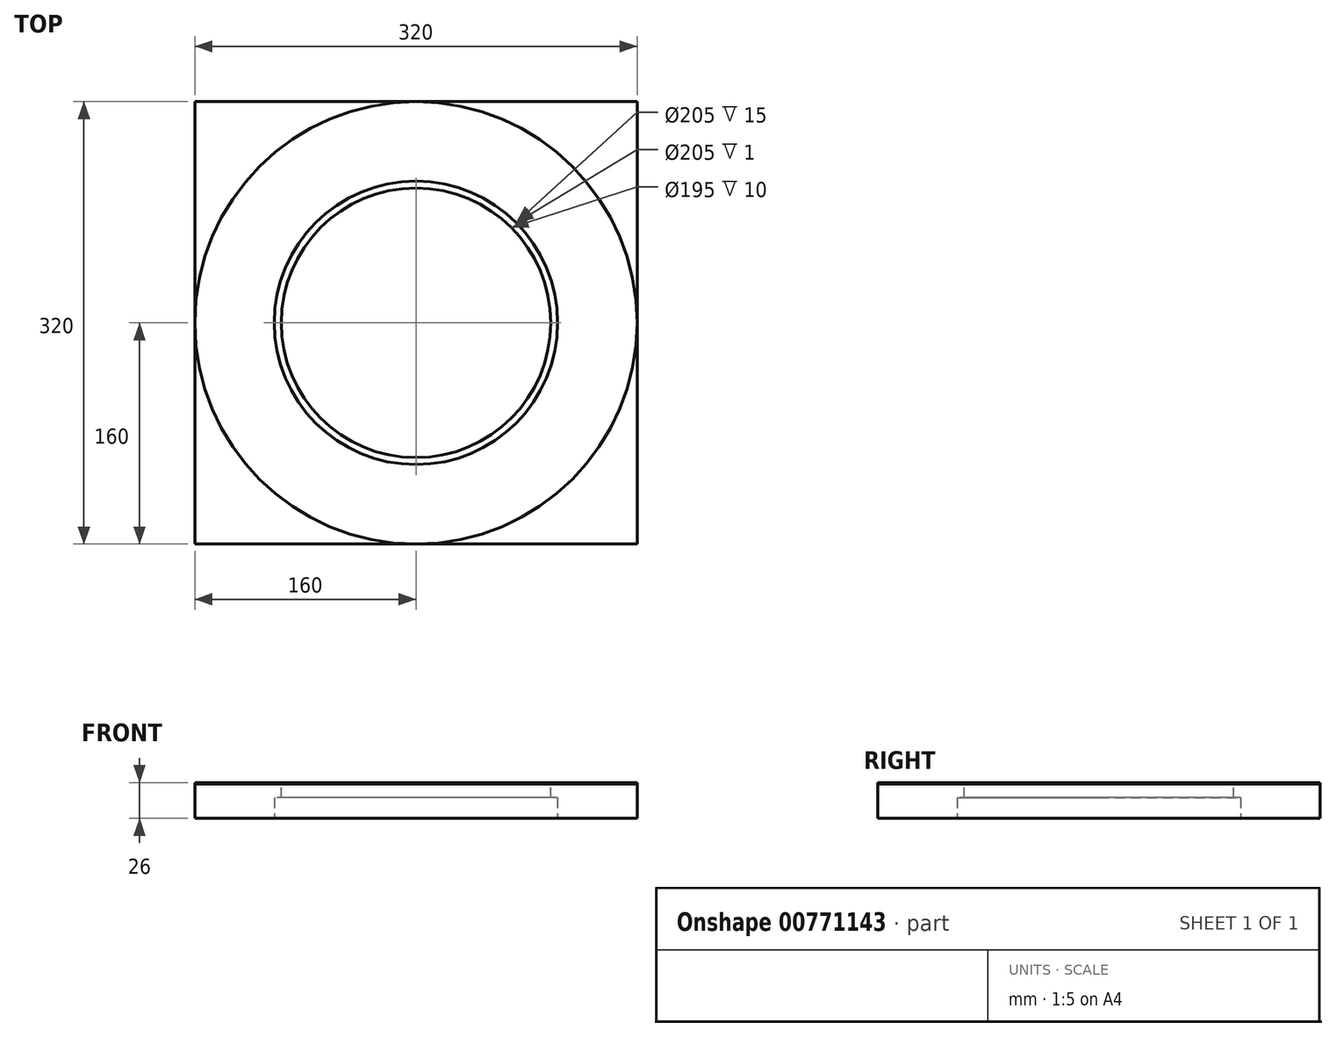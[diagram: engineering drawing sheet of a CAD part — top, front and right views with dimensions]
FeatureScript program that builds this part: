
annotation { "Feature Type Name" : "Feature", "Feature Type Description" : "" }
export const myFeature = defineFeature(function(context is Context, id is Id, definition is map)
    precondition{}
    {
        {
            var Q0;
            Q0=qCreatedBy(makeId("Top.planeOp"),FACE);
            var sketch = newSketch(context, id + "F0", { "sketchPlane" : qUnion([Q0])});
            skLineSegment(sketch, "E0.bottom", {"start": v(-160, 160) * mm, "end": v(160, 160) * mm});
            skLineSegment(sketch, "E0.top", {"start": v(-160, -160) * mm, "end": v(160, -160) * mm});
            skLineSegment(sketch, "E0.left", {"start": v(-160, 160) * mm, "end": v(-160, -160) * mm});
            skLineSegment(sketch, "E0.right", {"start": v(160, 160) * mm, "end": v(160, -160) * mm});
            skPoint(sketch, "E0.middle", {"position": v(0, 0) * mm});
            skCircle(sketch, "E1", {"center": v(0, 0) * mm, "radius": 102.5 * mm});
            skCircle(sketch, "E2", {"center": v(0, 0) * mm, "radius": 160 * mm});
            skSolve(sketch);
        }
        {
            var Q0;
            {var subQ0=sQuery(id+"F0.wireOp",EDGE,"E0.right");var subQ1=sQuery(id+"F0.wireOp",EDGE,"E0.bottom");var subQ2=makeQuery(id+"F0.imprint","INTERSECT",VERTEX,{"derivedFrom":[subQ1,subQ0]});Q0=makeQuery(id+"F0.imprint","IMPRINT",FACE,{"disambiguationData":[TD([[makeQuery(id+"F0.imprint","IMPRINT",EDGE,{"disambiguationData":[TD([[subQ2,1.0]])],"derivedFrom":subQ1}),-1.0]])]});}
            var Q1;
            Q1=makeQuery(id+"F0.imprint","IMPRINT",FACE,{"disambiguationData":[TD([[makeQuery(id+"F0.imprint","IMPRINT",EDGE,{"derivedFrom":sQuery(id+"F0.wireOp",EDGE,"E1")}),-1.0]])]});
            var Q2;
            {var subQ0=sQuery(id+"F0.wireOp",EDGE,"E0.right");var subQ1=sQuery(id+"F0.wireOp",EDGE,"E0.top");var subQ2=makeQuery(id+"F0.imprint","INTERSECT",VERTEX,{"derivedFrom":[subQ1,subQ0]});Q2=makeQuery(id+"F0.imprint","IMPRINT",FACE,{"disambiguationData":[TD([[makeQuery(id+"F0.imprint","IMPRINT",EDGE,{"disambiguationData":[TD([[subQ2,1.0]])],"derivedFrom":subQ1}),1.0]])]});}
            var Q3;
            Q3=makeQuery(id+"F0.imprint","IMPRINT",FACE,{"disambiguationData":[TD([[makeQuery(id+"F0.imprint","IMPRINT",EDGE,{"derivedFrom":sQuery(id+"F0.wireOp",EDGE,"E1")}),1.0]])]});
            var Q4;
            {var subQ0=sQuery(id+"F0.wireOp",EDGE,"E0.left");var subQ1=sQuery(id+"F0.wireOp",EDGE,"E0.bottom");var subQ2=makeQuery(id+"F0.imprint","INTERSECT",VERTEX,{"derivedFrom":[subQ1,subQ0]});Q4=makeQuery(id+"F0.imprint","IMPRINT",FACE,{"disambiguationData":[TD([[makeQuery(id+"F0.imprint","IMPRINT",EDGE,{"disambiguationData":[TD([[subQ2,-1.0]])],"derivedFrom":subQ1}),-1.0]])]});}
            var Q5;
            {var subQ0=sQuery(id+"F0.wireOp",EDGE,"E0.left");var subQ1=sQuery(id+"F0.wireOp",EDGE,"E0.top");var subQ2=makeQuery(id+"F0.imprint","INTERSECT",VERTEX,{"derivedFrom":[subQ1,subQ0]});Q5=makeQuery(id+"F0.imprint","IMPRINT",FACE,{"disambiguationData":[TD([[makeQuery(id+"F0.imprint","IMPRINT",EDGE,{"disambiguationData":[TD([[subQ2,-1.0]])],"derivedFrom":subQ1}),1.0]])]});}
            extrude(context, id + "F1", {"entities" : qUnion([Q0, Q1, Q2, Q3, Q4, Q5]), "oppositeDirection" : true, "depth" : 25 * mm, "offsetDistance" : 25 * mm});
        }
        {
            var Q0;
            Q0=makeQuery(id+"F0.imprint","IMPRINT",FACE,{"disambiguationData":[TD([[makeQuery(id+"F0.imprint","IMPRINT",EDGE,{"derivedFrom":sQuery(id+"F0.wireOp",EDGE,"E1")}),-1.0]])]});
            extrude(context, id + "F2", {"entities" : qUnion([Q0]), "operationType" : NewBodyOperationType.ADD, "depth" : 1 * mm, "offsetDistance" : 25 * mm});
        }
        {
            var Q0;
            Q0=makeQuery(id+"F2.boolean.opBoolean","SPLIT",FACE,{"disambiguationData":[TD([makeQuery(id+"F2.opExtrude","SWEPT_FACE",FACE,{"disambiguationData":[OSD([sQuery(id+"F0.wireOp",EDGE,"E1")])]})])],"derivedFrom":makeQuery(id+"F1.opExtrude","CAP_FACE",FACE,{"disambiguationData":[OSD([sQuery(id+"F0.wireOp",EDGE,"E0.bottom"),sQuery(id+"F0.wireOp",EDGE,"E0.top"),sQuery(id+"F0.wireOp",EDGE,"E0.left"),sQuery(id+"F0.wireOp",EDGE,"E0.right")])],"isStart":true})});
            extrude(context, id + "F3", {"entities" : qUnion([Q0]), "operationType" : NewBodyOperationType.REMOVE, "oppositeDirection" : true, "depth" : 25 * mm, "offsetDistance" : 25 * mm});
        }
        {
            var Q0;
            Q0=qCreatedBy(makeId("Top.planeOp"),FACE);
            var sketch = newSketch(context, id + "F4", { "sketchPlane" : qUnion([Q0])});
            skCircle(sketch, "E3", {"center": v(0, 0) * mm, "radius": 97.5 * mm});
            skCircle(sketch, "E4", {"center": v(0, 0) * mm, "radius": 102.5 * mm});
            skSolve(sketch);
        }
        {
            var Q0;
            Q0=makeQuery(id+"F4.imprint","IMPRINT",FACE,{"disambiguationData":[TD([[makeQuery(id+"F4.imprint","IMPRINT",EDGE,{"derivedFrom":sQuery(id+"F4.wireOp",EDGE,"E3")}),-1.0]])]});
            extrude(context, id + "F5", {"entities" : qUnion([Q0]), "operationType" : NewBodyOperationType.ADD, "oppositeDirection" : true, "depth" : 10 * mm, "offsetDistance" : 25 * mm});
        }
    });
